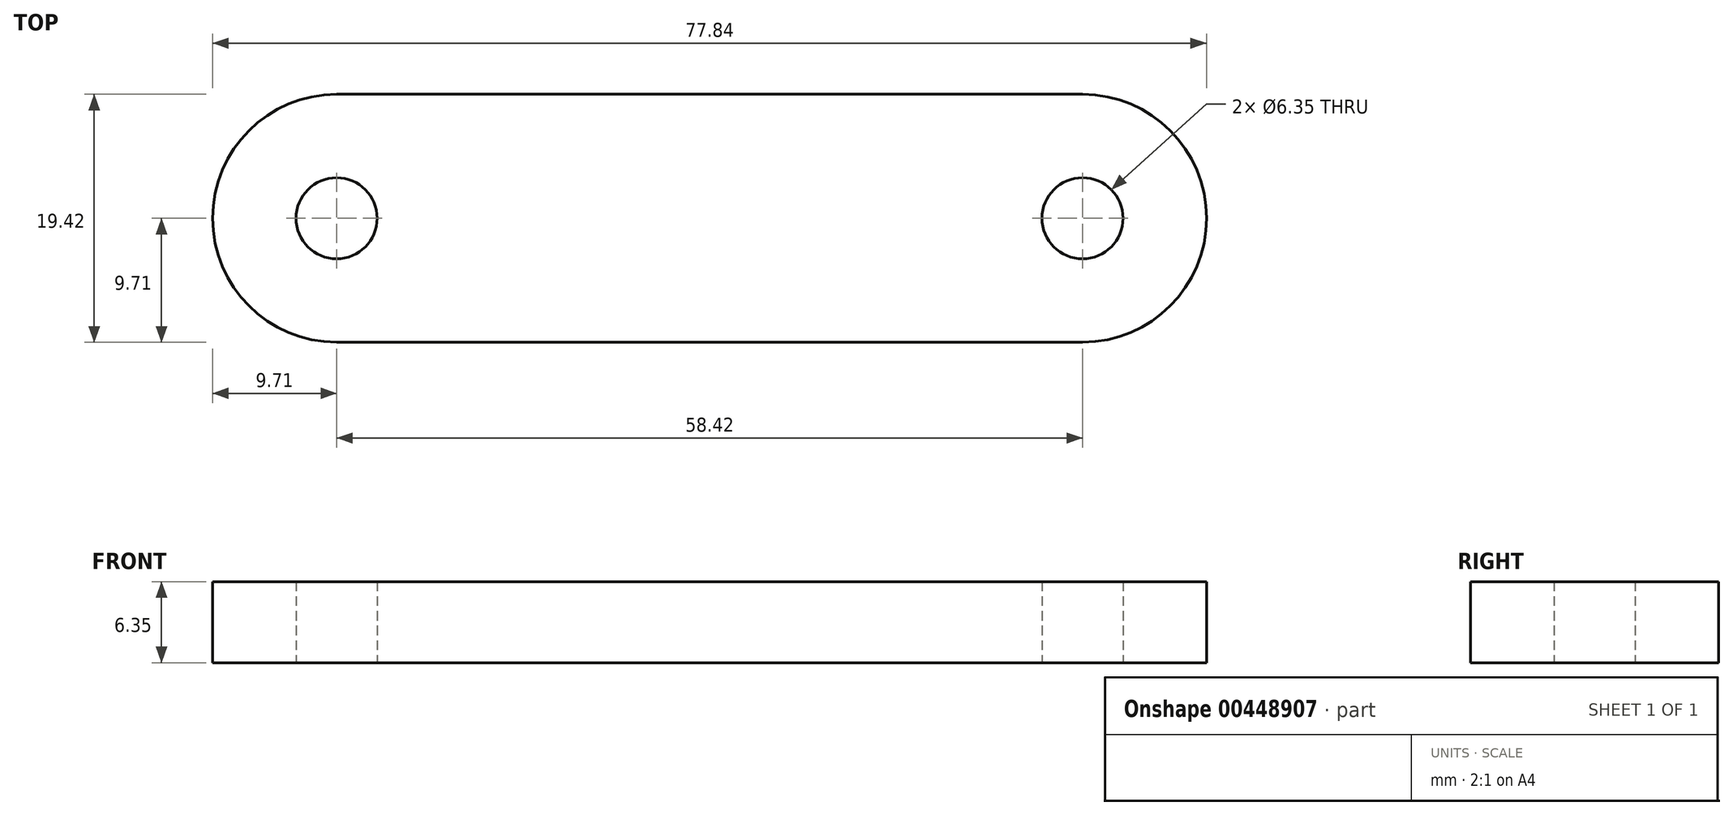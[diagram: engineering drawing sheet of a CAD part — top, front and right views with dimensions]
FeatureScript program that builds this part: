
annotation { "Feature Type Name" : "Feature", "Feature Type Description" : "" }
export const myFeature = defineFeature(function(context is Context, id is Id, definition is map)
    precondition{}
    {
        {
            var Q0;
            Q0=qCreatedBy(makeId("Top.planeOp"),FACE);
            var sketch = newSketch(context, id + "F0", { "sketchPlane" : qUnion([Q0])});
            skArc(sketch, "E0", {"start": v(-29.21, 9.7) * mm, "mid": v(-38.92, 0) * mm, "end": v(-29.21, -9.7) * mm});
            skArc(sketch, "E1", {"start": v(29.21, -9.7) * mm, "mid": v(38.92, 0) * mm, "end": v(29.21, 9.7) * mm});
            skLineSegment(sketch, "E2", {"start": v(-29.21, 9.7) * mm, "end": v(29.21, 9.7) * mm});
            skLineSegment(sketch, "E3", {"start": v(-29.21, -9.7) * mm, "end": v(29.21, -9.7) * mm});
            skCircle(sketch, "E4", {"center": v(-29.21, 0) * mm, "radius": 3.18 * mm});
            skCircle(sketch, "E5", {"center": v(29.21, 0) * mm, "radius": 3.18 * mm});
            skSolve(sketch);
        }
        {
            var Q0;
            Q0 = qSketchRegion(id + "F0", true);
            extrude(context, id + "F1", {"entities" : qUnion([Q0]), "depth" : 6.35 * mm});
        }
    });
